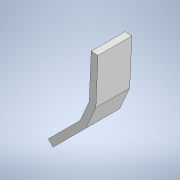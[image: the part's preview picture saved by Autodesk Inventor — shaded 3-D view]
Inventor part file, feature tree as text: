
AUTODESK INVENTOR PART (.ipt)
format: ipt  version: 2020 (Build 240168000, 168)  size: 121,344 bytes
history: native  units: mm
features: other x5, reference x2, extrude x1, plane x1, sketch x1
ambient origin geometry x8: Origin, YZ Plane, XZ Plane, XY Plane, X Axis, Y Axis, Z Axis, Center Point
bodies: Solid1 (feature_tree)
feature tree (10):
  extrude  "Extrusion1"  Depth=15.0mm
  plane  "Work Plane1"
  sketch  "Sketch1"  dims[d0=20.0mm d1=10.0mm d2=20.0mm d3=3.0mm d4=3.0mm d5=3.0mm d6=15.0mm d7=0.0mm]
  reference  "Reference1"
  reference  "Reference2"
  parser-record x1  (decoder bookkeeping rows leaked as tree rows — omitted from the tree; the rows remain in map.json)
  other  "leg_1.iam"
  other  "reducer_1:1"
  other  "mot_holder_1:1"
  other  "reducer_1:2"
note: 1 file-system path scrubbed to <path> (originals preserved in map.json)
